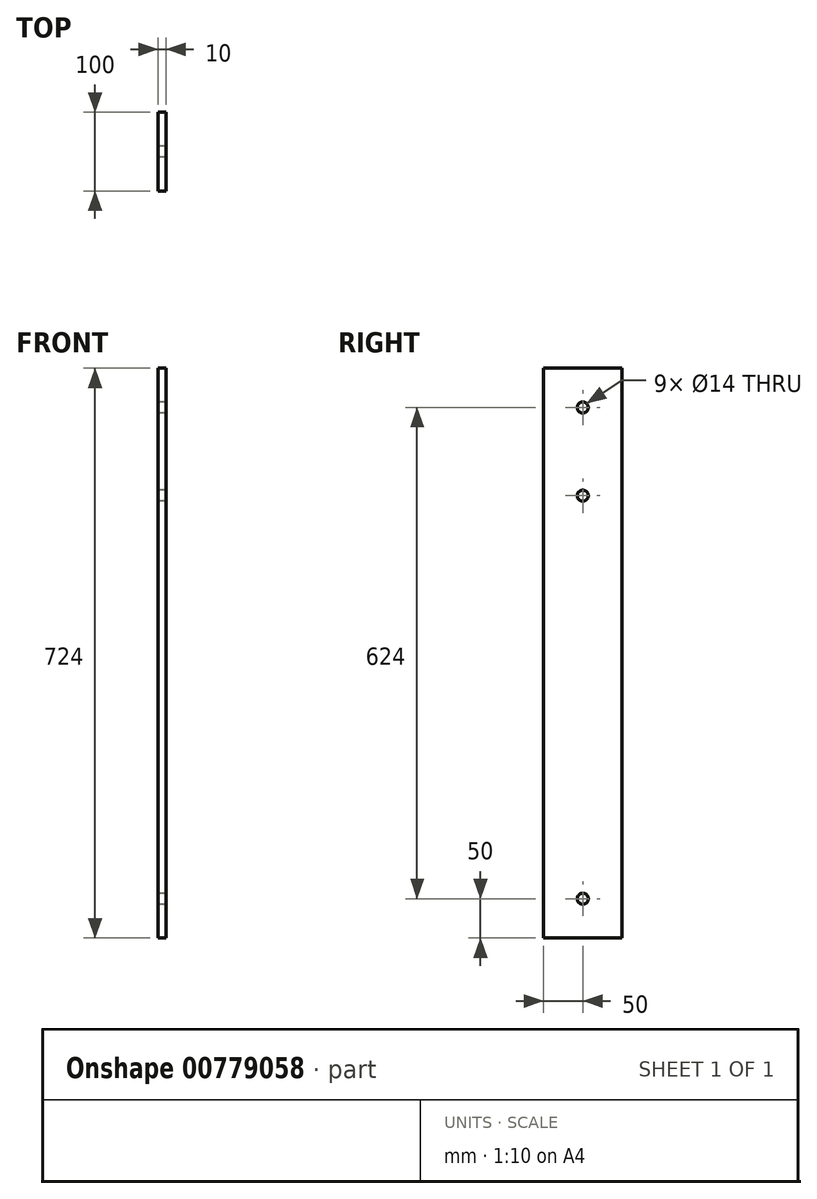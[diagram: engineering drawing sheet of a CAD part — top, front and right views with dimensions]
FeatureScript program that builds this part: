
annotation { "Feature Type Name" : "Feature", "Feature Type Description" : "" }
export const myFeature = defineFeature(function(context is Context, id is Id, definition is map)
    precondition{}
    {
        {
            var Q0;
            Q0=qCreatedBy(makeId("Right.planeOp"),FACE);
            var sketch = newSketch(context, id + "F0", { "sketchPlane" : qUnion([Q0])});
            skLineSegment(sketch, "E0.bottom", {"start": v(50, 362) * mm, "end": v(-50, 362) * mm});
            skLineSegment(sketch, "E0.top", {"start": v(50, -362) * mm, "end": v(-50, -362) * mm});
            skLineSegment(sketch, "E0.left", {"start": v(50, 362) * mm, "end": v(50, -362) * mm});
            skLineSegment(sketch, "E0.right", {"start": v(-50, 362) * mm, "end": v(-50, -362) * mm});
            skPoint(sketch, "E0.middle", {"position": v(0, 0) * mm});
            skCircle(sketch, "E1", {"center": v(0, -312) * mm, "radius": 7 * mm});
            skCircle(sketch, "E2", {"center": v(0, 312) * mm, "radius": 7 * mm});
            skCircle(sketch, "E3", {"center": v(0, 200) * mm, "radius": 7 * mm});
            skSolve(sketch);
        }
        {
            var Q0;
            Q0=makeQuery(id+"F0.imprint","IMPRINT",FACE,{"disambiguationData":[TD([[makeQuery(id+"F0.imprint","IMPRINT",EDGE,{"derivedFrom":sQuery(id+"F0.wireOp",EDGE,"E0.bottom")}),1.0]])]});
            extrude(context, id + "F1", {"entities" : qUnion([Q0]), "depth" : 10 * mm, "offsetDistance" : 25 * mm});
        }
    });
